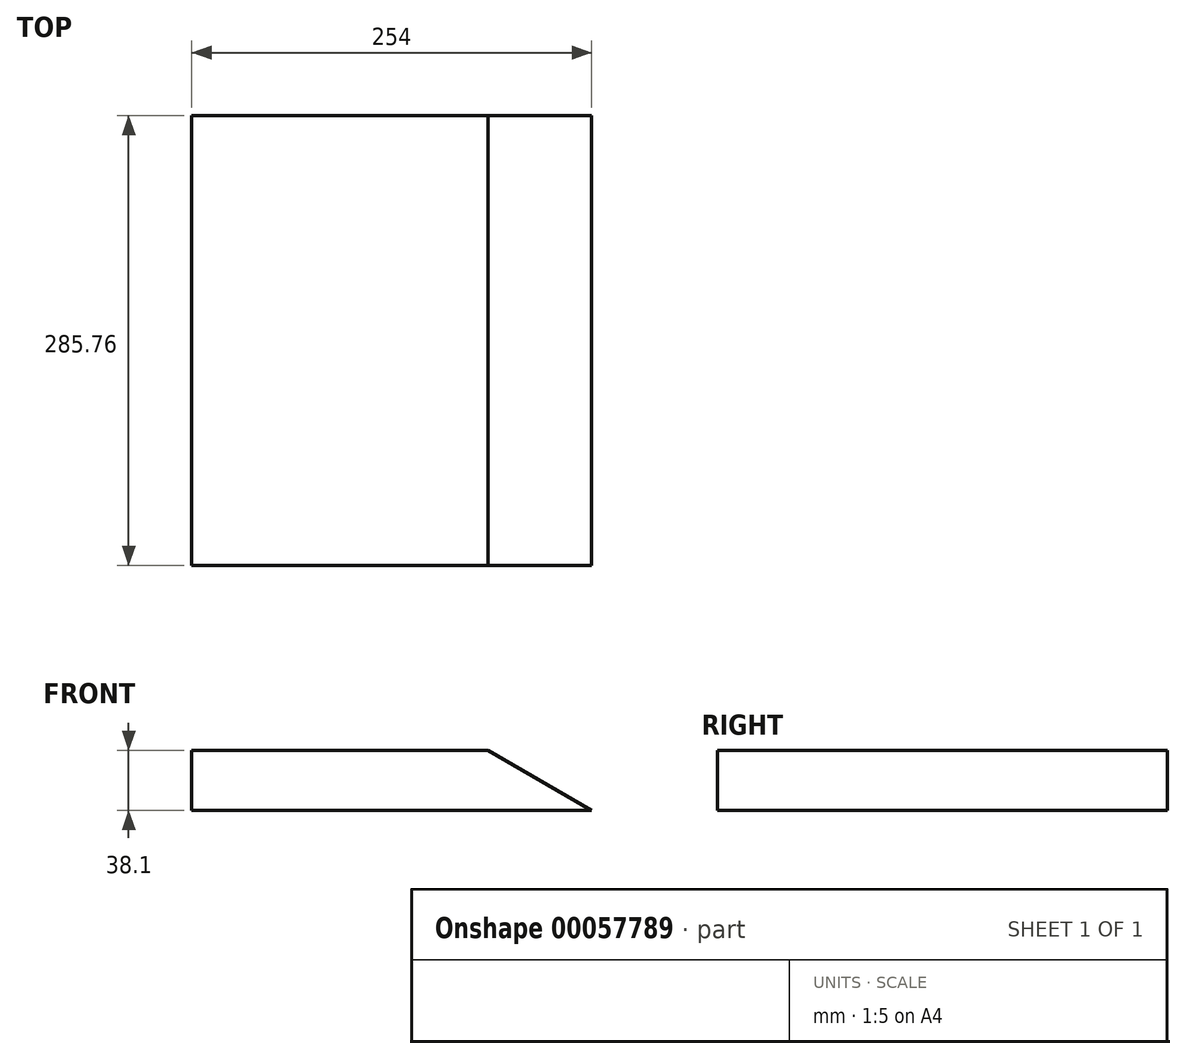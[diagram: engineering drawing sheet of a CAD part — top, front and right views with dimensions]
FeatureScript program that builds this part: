
annotation { "Feature Type Name" : "Feature", "Feature Type Description" : "" }
export const myFeature = defineFeature(function(context is Context, id is Id, definition is map)
    precondition{}
    {
        {
            var Q0;
            Q0=qCreatedBy(makeId("Right.planeOp"),FACE);
            var sketch = newSketch(context, id + "F0", { "sketchPlane" : qUnion([Q0])});
            skLineSegment(sketch, "E0.rect.bottom", {"start": v(142.88, -19.05) * mm, "end": v(-142.87, -19.05) * mm});
            skLineSegment(sketch, "E0.rect.top", {"start": v(142.88, 19.05) * mm, "end": v(-142.87, 19.05) * mm});
            skLineSegment(sketch, "E0.rect.left", {"start": v(142.88, -19.05) * mm, "end": v(142.88, 19.05) * mm});
            skLineSegment(sketch, "E0.rect.right", {"start": v(-142.87, -19.05) * mm, "end": v(-142.87, 19.05) * mm});
            skPoint(sketch, "E0.rect.middle", {"position": v(0, 0) * mm});
            skSolve(sketch);
        }
        {
            var Q0;
            Q0 = qSketchRegion(id + "F0", true);
            extrude(context, id + "F1", {"entities" : qUnion([Q0]), "endBound" : BoundingType.SYMMETRIC, "depth" : 254 * mm});
        }
        {
            var Q0;
            Q0=qCreatedBy(makeId("Front.planeOp"),FACE);
            var sketch = newSketch(context, id + "F2", { "sketchPlane" : qUnion([Q0])});
            skLineSegment(sketch, "E1", {"start": v(17.01, 44.45) * mm, "end": v(152.4, 44.45) * mm});
            skLineSegment(sketch, "E2", {"start": v(152.4, 44.45) * mm, "end": v(152.4, -33.71) * mm});
            skLineSegment(sketch, "E3", {"start": v(152.4, -33.71) * mm, "end": v(17.01, 44.45) * mm});
            skSolve(sketch);
        }
        {
            var Q0;
            Q0 = qSketchRegion(id + "F2", true);
            extrude(context, id + "F3", {"entities" : qUnion([Q0]), "operationType" : NewBodyOperationType.REMOVE, "endBound" : BoundingType.SYMMETRIC, "depth" : 406.4 * mm});
        }
    });
